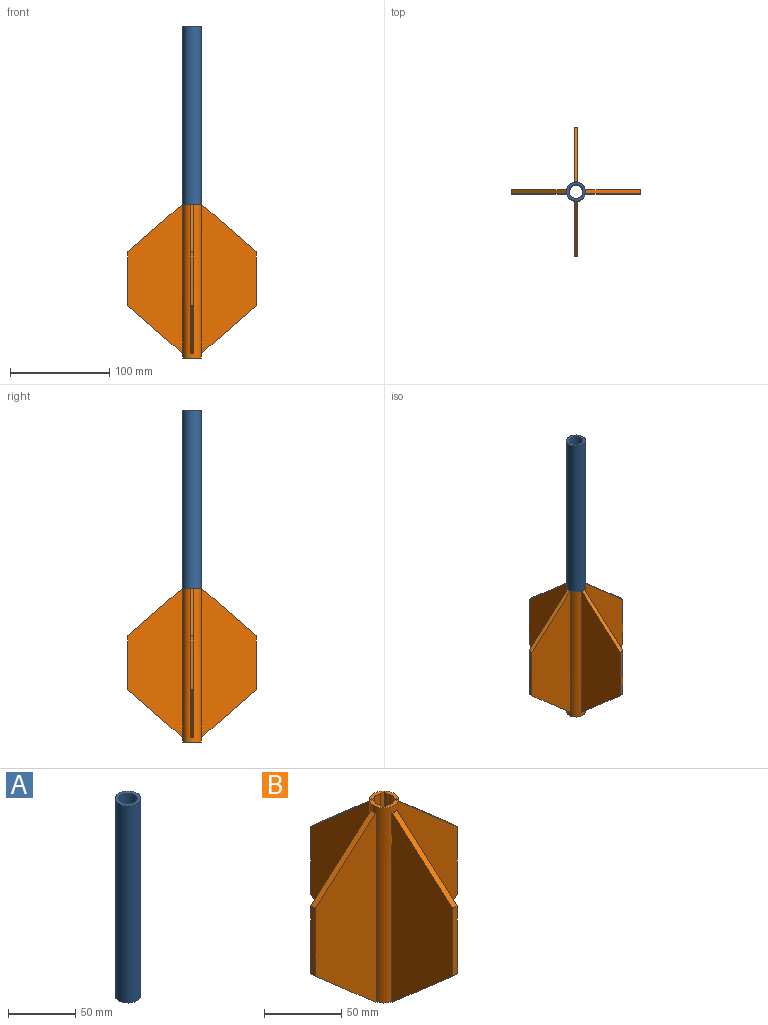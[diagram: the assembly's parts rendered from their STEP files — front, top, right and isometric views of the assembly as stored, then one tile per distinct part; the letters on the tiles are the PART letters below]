
ASSEMBLY  parts=2 mates=1
PART A: 4 faces, bbox 19.2x19.2x180 mm
  f0: cylinder r=9.6mm len=180mm, axis (0,0,-1), area 10857.3mm2, adj f1,f2
  f1: plane 19.2x19.2mm, normal (0,0,1), area 141mm2, adj f0,f3
  f2: plane 19.2x19.2mm, normal (0,0,-1), area 141mm2, adj f0,f3
  f3: cylinder r=6.88mm len=180mm, axis (0,0,1), area 7775.4mm2, adj f1,f2
PART B: 40 faces, bbox 130x130x155 mm
  f0: plane 19.05x19.05mm, normal (0,0,1), area 128.5mm2, adj f1,f27,f28,f29,f31,f32,f34,f35
  f1: cylinder r=9.53mm len=155mm, axis (0,0,-1), area 6858.3mm2, adj f0,f2,f3,f4,f6,f9,f10,f12
  f2: plane 20x20mm, normal (0,0,-1), area 150.6mm2, adj f1,f3,f4,f8,f9,f10,f14,f15
  f3: plane 150x55.69mm, normal (1,0,0), area 5713.1mm2, adj f1,f2,f5,f6,f7,f8
  f4: plane 150x55.69mm, normal (-1,0,0), area 5713.1mm2, adj f1,f2,f5,f6,f7,f8
  f5: plane 54x4mm, normal (0,1,0), area 216mm2, adj f3,f4,f7,f8
  f6: plane 4x0.69mm, normal (0,0,1), area 2.2mm2, adj f1,f3,f4,f7
  f7: plane 55x48mm, normal (0,0.66,0.75), area 292mm2, adj f3,f4,f5,f6
  f8: plane 55x48mm, normal (0,0.66,-0.75), area 292mm2, adj f2,f3,f4,f5
  f9: plane 150x55.69mm, normal (0,1,0), area 5713.1mm2, adj f1,f2,f11,f12,f13,f14
  f10: plane 150x55.69mm, normal (0,-1,0), area 5713.1mm2, adj f1,f2,f11,f12,f13,f14
  f11: plane 54x4mm, normal (-1,0,0), area 216mm2, adj f9,f10,f13,f14
  f12: plane 4x0.69mm, normal (0,0,1), area 2.2mm2, adj f1,f9,f10,f13
  f13: plane 55x48mm, normal (-0.66,0,0.75), area 292mm2, adj f9,f10,f11,f12
  f14: plane 55x48mm, normal (-0.66,0,-0.75), area 292mm2, adj f2,f9,f10,f11
  f15: plane 150x55.69mm, normal (-1,0,0), area 5713.1mm2, adj f1,f2,f17,f18,f19,f20
  f16: plane 150x55.69mm, normal (1,0,0), area 5713.1mm2, adj f1,f2,f17,f18,f19,f20
  f17: plane 54x4mm, normal (0,-1,0), area 216mm2, adj f15,f16,f19,f20
  f18: plane 4x0.69mm, normal (0,0,1), area 2.2mm2, adj f1,f15,f16,f19
  f19: plane 55x48mm, normal (0,-0.66,0.75), area 292mm2, adj f15,f16,f17,f18
  f20: plane 55x48mm, normal (0,-0.66,-0.75), area 292mm2, adj f2,f15,f16,f17
  f21: plane 150x55.69mm, normal (0,-1,0), area 5713.1mm2, adj f1,f2,f23,f24,f25,f26
  f22: plane 150x55.69mm, normal (0,1,0), area 5713.1mm2, adj f1,f2,f23,f24,f25,f26
  f23: plane 54x4mm, normal (1,0,0), area 216mm2, adj f21,f22,f25,f26
  f24: plane 4x0.69mm, normal (0,0,1), area 2.2mm2, adj f1,f21,f22,f25
  f25: plane 55x48mm, normal (0.66,0,0.75), area 292mm2, adj f21,f22,f23,f24
  f26: plane 55x48mm, normal (0.66,0,-0.75), area 292mm2, adj f2,f21,f22,f23
  f27: cylinder r=6.75mm len=155mm, axis (0,0,1), area 5988.8mm2, adj f0,f2,f28,f29,f30,f31,f32,f33
  f28: plane 35x2.91mm, normal (0,-1,0), area 101.8mm2, adj f0,f27,f29,f30
  f29: plane 35x2.91mm, normal (1,0,0), area 101.8mm2, adj f0,f27,f28,f30
  f30: plane 2.91x2.91mm, normal (0,0,1), area 3.3mm2, adj f27,f28,f29
  f31: plane 35x2.91mm, normal (0,1,0), area 101.8mm2, adj f0,f27,f32,f33
  f32: plane 35x2.91mm, normal (-1,0,0), area 101.8mm2, adj f0,f27,f31,f33
  f33: plane 2.91x2.91mm, normal (0,0,1), area 3.3mm2, adj f27,f31,f32
  f34: plane 35x2.91mm, normal (1,0,0), area 101.8mm2, adj f0,f27,f35,f36
  f35: plane 35x2.91mm, normal (0,1,0), area 101.8mm2, adj f0,f27,f34,f36
  f36: plane 2.91x2.91mm, normal (0,0,1), area 3.3mm2, adj f27,f34,f35
  f37: plane 35x2.91mm, normal (0,-1,0), area 101.8mm2, adj f0,f27,f38,f39
  f38: plane 35x2.91mm, normal (-1,0,0), area 101.8mm2, adj f0,f27,f37,f39
  f39: plane 2.91x2.91mm, normal (0,0,1), area 3.3mm2, adj f27,f37,f38
PLACE A t=(-88.39,-57.6,36.86)mm
PLACE B rot(axis=(-1,0,0),180deg) t=(-88.39,-57.6,36.86)mm
MATE fastened A.f3 <-> B.f27  axis (0,0,1) through (-88.39,-57.6,36.86)mm
